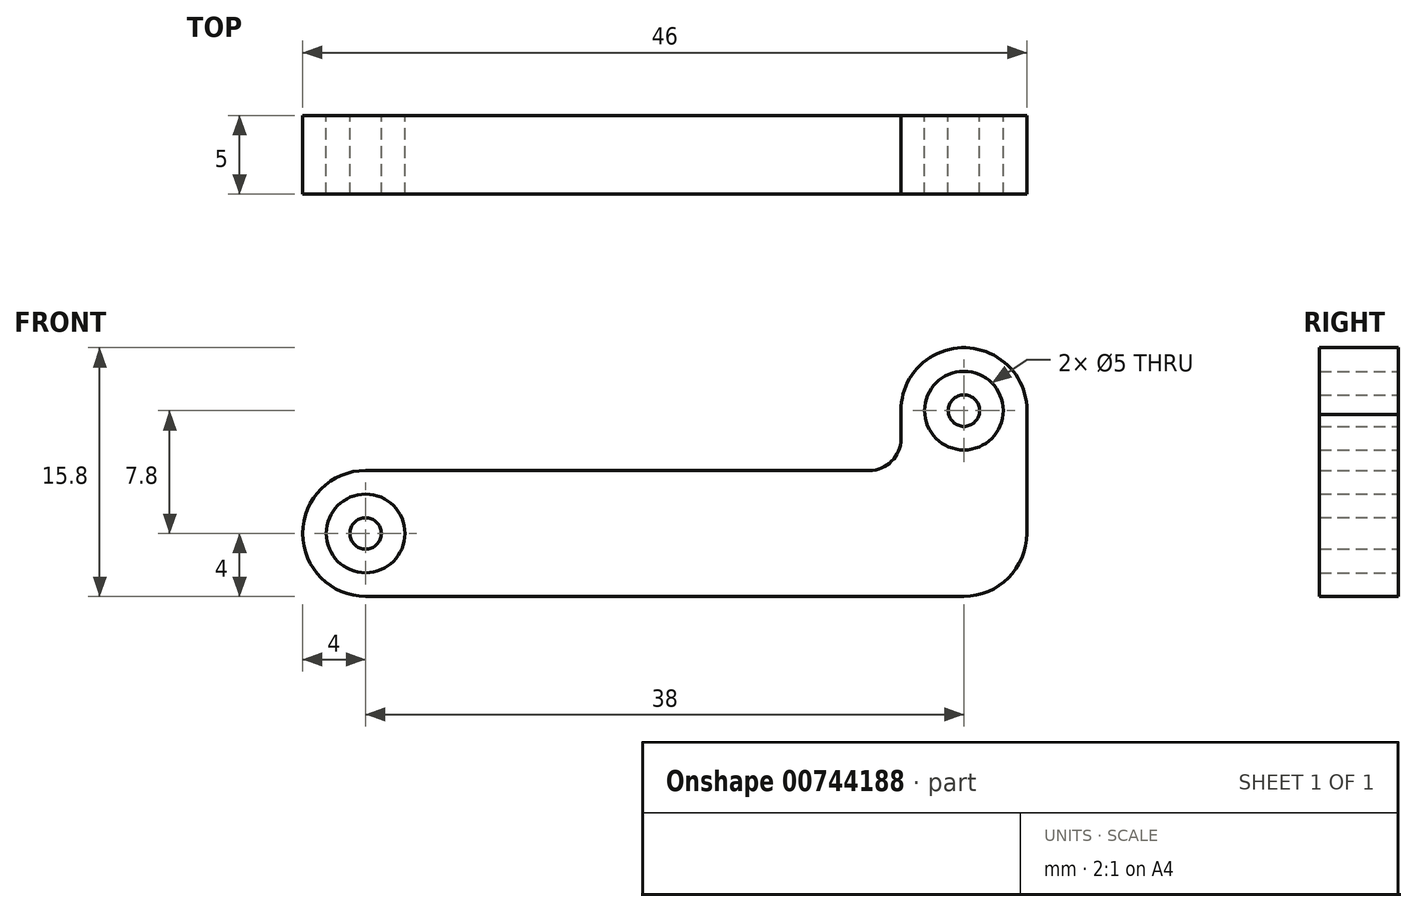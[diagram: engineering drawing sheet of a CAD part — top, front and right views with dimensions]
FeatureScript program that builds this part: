
annotation { "Feature Type Name" : "Feature", "Feature Type Description" : "" }
export const myFeature = defineFeature(function(context is Context, id is Id, definition is map)
    precondition{}
    {
        {
            var Q0;
            Q0=qCreatedBy(makeId("Front.planeOp"),FACE);
            var sketch = newSketch(context, id + "F0", { "sketchPlane" : qUnion([Q0])});
            skCircle(sketch, "E0", {"center": v(0, 0) * mm, "radius": 4 * mm});
            skCircle(sketch, "E1", {"center": v(0, 0) * mm, "radius": 2.5 * mm});
            skCircle(sketch, "E2", {"center": v(0, 0) * mm, "radius": 1 * mm});
            skCircle(sketch, "E3", {"center": v(38, 7.8) * mm, "radius": 4 * mm});
            skCircle(sketch, "E4", {"center": v(38, 7.8) * mm, "radius": 2.5 * mm});
            skCircle(sketch, "E5", {"center": v(38, 7.8) * mm, "radius": 1 * mm});
            skLineSegment(sketch, "E6", {"start": v(34, 7.8) * mm, "end": v(34, 6) * mm});
            skLineSegment(sketch, "E7", {"start": v(32, 4) * mm, "end": v(0, 4) * mm});
            skLineSegment(sketch, "E8", {"start": v(42, 8.04) * mm, "end": v(42, 0) * mm});
            skLineSegment(sketch, "E9", {"start": v(38, -4) * mm, "end": v(0, -4) * mm});
            skPoint(sketch, "E10.visualSharp", {"position": v(34, 4) * mm});
            skArc(sketch, "E10.filletArc", {"start": v(32, 4) * mm, "mid": v(33.41, 4.59) * mm, "end": v(34, 6) * mm});
            skPoint(sketch, "E11.visualSharp", {"position": v(42, -4) * mm});
            skArc(sketch, "E11.filletArc", {"start": v(38, -4) * mm, "mid": v(40.82, -2.83) * mm, "end": v(42, 0) * mm});
            skSolve(sketch);
        }
        {
            var Q0;
            Q0=qSketchRegion(id+"F0",true);
            var Q1;
            Q1=makeQuery(id+"F0.imprint","IMPRINT",FACE,{"disambiguationData":[TD([[makeQuery(id+"F0.imprint","IMPRINT",EDGE,{"derivedFrom":sQuery(id+"F0.wireOp",EDGE,"E2")}),1.0]])]});
            var Q2;
            Q2=makeQuery(id+"F0.imprint","IMPRINT",FACE,{"disambiguationData":[TD([[makeQuery(id+"F0.imprint","IMPRINT",EDGE,{"derivedFrom":sQuery(id+"F0.wireOp",EDGE,"E5")}),1.0]])]});
            extrude(context, id + "F1", {"entities" : qUnion([Q0, Q1, Q2]), "depth" : 5 * mm, "offsetDistance" : 25 * mm});
        }
    });
